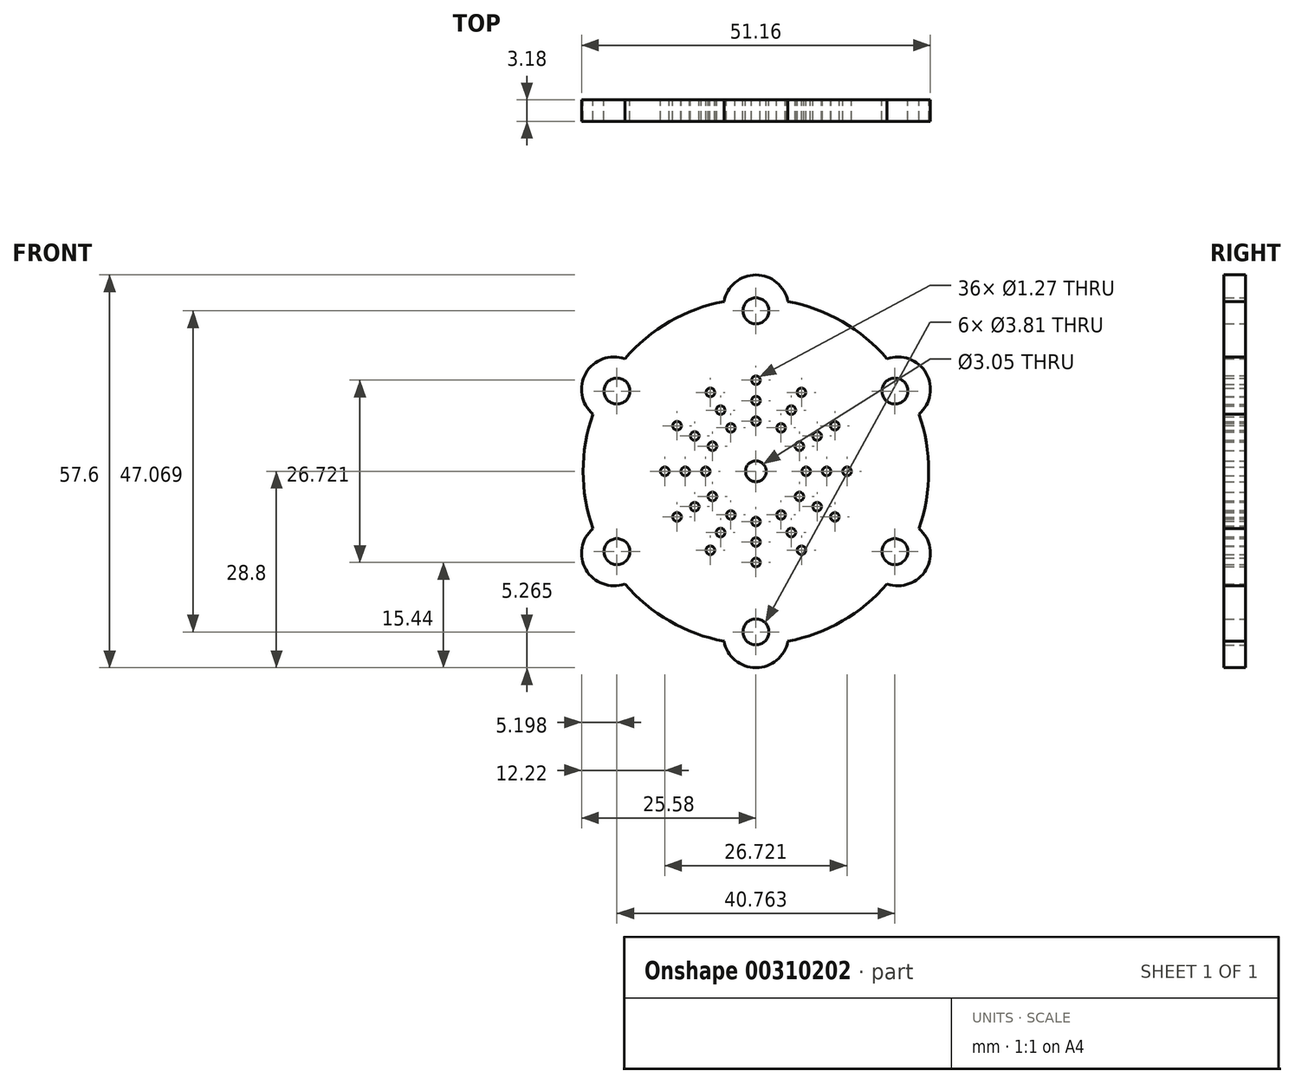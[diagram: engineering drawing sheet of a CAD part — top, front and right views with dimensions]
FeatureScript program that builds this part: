
annotation { "Feature Type Name" : "Feature", "Feature Type Description" : "" }
export const myFeature = defineFeature(function(context is Context, id is Id, definition is map)
    precondition{}
    {
        {
            var Q0;
            Q0=qCreatedBy(makeId("Front.planeOp"),FACE);
            var sketch = newSketch(context, id + "F0", { "sketchPlane" : qUnion([Q0])});
            skPoint(sketch, "E0.center", {"position": v(0, 0) * mm});
            skCircle(sketch, "E1", {"center": v(0, 0) * mm, "radius": 1.52 * mm});
            skCircle(sketch, "E2", {"center": v(0, 7.37) * mm, "radius": 0.64 * mm});
            skCircle(sketch, "E3", {"center": v(0, 10.36) * mm, "radius": 0.64 * mm});
            skCircle(sketch, "E4", {"center": v(0, 13.36) * mm, "radius": 0.64 * mm});
            skCircle(sketch, "E5.1.1", {"center": v(-13.36, 0) * mm, "radius": 0.64 * mm});
            skCircle(sketch, "E5.1.2", {"center": v(-10.36, 0) * mm, "radius": 0.64 * mm});
            skCircle(sketch, "E5.1.3", {"center": v(-7.37, 0) * mm, "radius": 0.64 * mm});
            skCircle(sketch, "E5.2.1", {"center": v(0, -13.36) * mm, "radius": 0.64 * mm});
            skCircle(sketch, "E5.2.2", {"center": v(0, -10.36) * mm, "radius": 0.64 * mm});
            skCircle(sketch, "E5.2.3", {"center": v(0, -7.37) * mm, "radius": 0.64 * mm});
            skCircle(sketch, "E5.3.1", {"center": v(13.36, 0) * mm, "radius": 0.64 * mm});
            skCircle(sketch, "E5.3.2", {"center": v(10.36, 0) * mm, "radius": 0.64 * mm});
            skCircle(sketch, "E5.3.3", {"center": v(7.37, 0) * mm, "radius": 0.64 * mm});
            skCircle(sketch, "E6.1.0", {"center": v(6.38, -3.68) * mm, "radius": 0.64 * mm});
            skCircle(sketch, "E6.1.1", {"center": v(8.97, -5.18) * mm, "radius": 0.64 * mm});
            skCircle(sketch, "E6.1.2", {"center": v(11.57, -6.68) * mm, "radius": 0.64 * mm});
            skCircle(sketch, "E6.2.0", {"center": v(6.38, 3.68) * mm, "radius": 0.64 * mm});
            skCircle(sketch, "E6.2.1", {"center": v(8.97, 5.18) * mm, "radius": 0.64 * mm});
            skCircle(sketch, "E6.2.2", {"center": v(11.57, 6.68) * mm, "radius": 0.64 * mm});
            skCircle(sketch, "E6.4.0", {"center": v(-6.38, 3.68) * mm, "radius": 0.64 * mm});
            skCircle(sketch, "E6.4.1", {"center": v(-8.97, 5.18) * mm, "radius": 0.64 * mm});
            skCircle(sketch, "E6.4.2", {"center": v(-11.57, 6.68) * mm, "radius": 0.64 * mm});
            skCircle(sketch, "E6.5.0", {"center": v(-6.38, -3.68) * mm, "radius": 0.64 * mm});
            skCircle(sketch, "E6.5.1", {"center": v(-8.97, -5.18) * mm, "radius": 0.64 * mm});
            skCircle(sketch, "E6.5.2", {"center": v(-11.57, -6.68) * mm, "radius": 0.64 * mm});
            skCircle(sketch, "E7.1.0", {"center": v(-3.68, -6.38) * mm, "radius": 0.64 * mm});
            skCircle(sketch, "E7.1.1", {"center": v(-5.18, -8.97) * mm, "radius": 0.64 * mm});
            skCircle(sketch, "E7.1.2", {"center": v(-6.68, -11.57) * mm, "radius": 0.64 * mm});
            skCircle(sketch, "E7.2.0", {"center": v(3.68, -6.38) * mm, "radius": 0.64 * mm});
            skCircle(sketch, "E7.2.1", {"center": v(5.18, -8.97) * mm, "radius": 0.64 * mm});
            skCircle(sketch, "E7.2.2", {"center": v(6.68, -11.57) * mm, "radius": 0.64 * mm});
            skCircle(sketch, "E7.4.0", {"center": v(3.68, 6.38) * mm, "radius": 0.64 * mm});
            skCircle(sketch, "E7.4.1", {"center": v(5.18, 8.97) * mm, "radius": 0.64 * mm});
            skCircle(sketch, "E7.4.2", {"center": v(6.68, 11.57) * mm, "radius": 0.64 * mm});
            skCircle(sketch, "E7.5.0", {"center": v(-3.68, 6.38) * mm, "radius": 0.64 * mm});
            skCircle(sketch, "E7.5.1", {"center": v(-5.18, 8.97) * mm, "radius": 0.64 * mm});
            skCircle(sketch, "E7.5.2", {"center": v(-6.68, 11.57) * mm, "radius": 0.64 * mm});
            skCircle(sketch, "E8", {"center": v(0, 23.53) * mm, "radius": 1.9 * mm});
            skArc(sketch, "E9", {"start": v(4.68, 24.9) * mm, "mid": v(0, 28.8) * mm, "end": v(-4.68, 24.9) * mm});
            skCircle(sketch, "E10.1.0", {"center": v(-20.38, 11.77) * mm, "radius": 1.9 * mm});
            skCircle(sketch, "E10.2.0", {"center": v(-20.38, -11.77) * mm, "radius": 1.9 * mm});
            skCircle(sketch, "E10.3.0", {"center": v(0, -23.53) * mm, "radius": 1.9 * mm});
            skCircle(sketch, "E10.4.0", {"center": v(20.38, -11.77) * mm, "radius": 1.9 * mm});
            skCircle(sketch, "E10.5.0", {"center": v(20.38, 11.77) * mm, "radius": 1.9 * mm});
            skArc(sketch, "E11", {"start": v(-23.91, 8.4) * mm, "mid": v(-25.34, 0) * mm, "end": v(-23.91, -8.4) * mm});
            skArc(sketch, "E12.1.0", {"start": v(-19.23, 16.5) * mm, "mid": v(-24.94, 14.4) * mm, "end": v(-23.91, 8.4) * mm});
            skArc(sketch, "E12.2.0", {"start": v(-23.91, -8.4) * mm, "mid": v(-24.94, -14.4) * mm, "end": v(-19.23, -16.5) * mm});
            skArc(sketch, "E12.3.0", {"start": v(-4.68, -24.9) * mm, "mid": v(0, -28.8) * mm, "end": v(4.68, -24.9) * mm});
            skArc(sketch, "E12.4.0", {"start": v(19.23, -16.5) * mm, "mid": v(24.94, -14.4) * mm, "end": v(23.91, -8.4) * mm});
            skArc(sketch, "E12.5.0", {"start": v(23.91, 8.4) * mm, "mid": v(24.94, 14.4) * mm, "end": v(19.23, 16.5) * mm});
            skArc(sketch, "E13.trimOffspring", {"start": v(-4.68, 24.9) * mm, "mid": v(-12.67, 21.95) * mm, "end": v(-19.23, 16.5) * mm});
            skArc(sketch, "E14.trimOffspring", {"start": v(19.23, 16.5) * mm, "mid": v(12.67, 21.95) * mm, "end": v(4.68, 24.9) * mm});
            skArc(sketch, "E15.trimOffspring", {"start": v(23.91, -8.4) * mm, "mid": v(25.34, 0) * mm, "end": v(23.91, 8.4) * mm});
            skArc(sketch, "E16.trimOffspring", {"start": v(-19.23, -16.5) * mm, "mid": v(-12.67, -21.95) * mm, "end": v(-4.68, -24.9) * mm});
            skArc(sketch, "E17.trimOffspring", {"start": v(4.68, -24.9) * mm, "mid": v(12.67, -21.95) * mm, "end": v(19.23, -16.5) * mm});
            skSolve(sketch);
        }
        {
            var Q0;
            Q0 = qSketchRegion(id + "F0", true);
            extrude(context, id + "F1", {"entities" : qUnion([Q0]), "depth" : 3.17 * mm});
        }
    });
